# Revit family: Desire_4_bp
name_source: partatom
category: Drzwi
revit_build: Autodesk Revit 2016 (Build: 20150714_1515(x64)
units: mm (PartAtom-declared; Revit-internal decimal feet)

## family parameters
Obiekt nadrzędny = Ściana
Punkt obliczania pomieszczeń = Nie
Tnij formami wycięć po wczytaniu = Nie
Współdzielony = Nie
Zawsze pionowo = Tak

## types (4) — shared parameters
Funkcja = Wewnętrzna
Konstrukcja analityczna = <Brak>
Model = Desire 4
Opis = Własność Porta KMI Poland, wszelkie prawa zastrzeżone.
Producent = PORTA KMI POLAND
URL = www.porta.com.pl
Zakończenie ściany = Wg obiektu nadrzędnego

## per-type parameters (varying)
| type | Hs | Sb | Ss | Szerokość | Szerokość brutto | Wysokość | Wysokość brutto |
| 80 cm x 202 cm | 2017 mm  [stored 6.61745 ft] | 846 mm  [stored 2.77559 ft] | 818 mm  [stored 2.68373 ft] | 800 mm  [stored 2.62467 ft] | 880 mm  [stored 2.88714 ft] | 2016 mm | 2060 mm  [stored 6.75853 ft] |
| 90 cm x 202 cm | 2017 mm  [stored 6.61745 ft] | 946 mm | 918 mm | 900 mm | 980 mm | 2016 mm | 2060 mm  [stored 6.75853 ft] |
| 80 cm x 220 cm | 2200 mm | 846 mm  [stored 2.77559 ft] | 818 mm  [stored 2.68373 ft] | 800 mm  [stored 2.62467 ft] | 880 mm  [stored 2.88714 ft] | 2200 mm | 2243 mm |
| 90 cm x 220 cm | 2200 mm | 946 mm | 918 mm | 900 mm | 980 mm | 2200 mm | 2243 mm |

note: [stored X ft] marks values corroborated as IEEE doubles in the binary element streams (Revit-internal decimal feet)

## geometry (parser evidence)
native form markers: Blend x4, Sweep x3
no freeform markers — native parametric forms only
